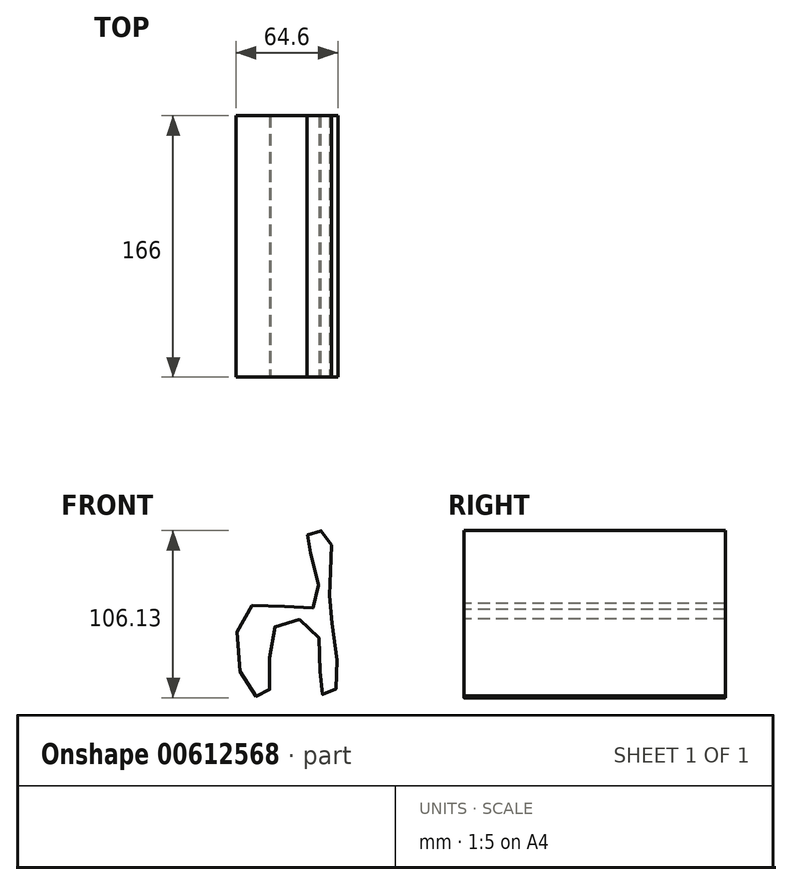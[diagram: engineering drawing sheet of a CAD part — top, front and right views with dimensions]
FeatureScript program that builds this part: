
annotation { "Feature Type Name" : "Feature", "Feature Type Description" : "" }
export const myFeature = defineFeature(function(context is Context, id is Id, definition is map)
    precondition{}
    {
        {
            var Q0;
            Q0=qCreatedBy(makeId("Front.planeOp"),FACE);
            var sketch = newSketch(context, id + "F0", { "sketchPlane" : qUnion([Q0])});
            skFitSpline(sketch, "E0", {"points": [v(44.42, 30.54) * mm, v(44.81, 0) * mm, v(46.61, -46.11) * mm, v(38.43, -46.71) * mm, v(35.03, -7.19) * mm, v(8.88, -4.8) * mm, v(4.7, -47.3) * mm, v(-8.28, -43.92) * mm, v(-7.09, 8.18) * mm, v(33.84, 7.59) * mm, v(31.04, 44.32) * mm, v(30.64, 54.7) * mm, v(41.62, 54.7) * mm, v(44.42, 30.54) * mm]});
            skSolve(sketch);
        }
        {
            var Q0;
            Q0=makeQuery(id+"F0.imprint","IMPRINT",FACE,{"disambiguationData":[TD([[makeQuery(id+"F0.imprint","IMPRINT",EDGE,{"derivedFrom":sQuery(id+"F0.wireOp",EDGE,"E0")}),-1.0]])]});
            var Q1;
            Q1=sQuery(id+"F0.wireOp",EDGE,"E0");
            extrude(context, id + "F1", {"entities" : qUnion([Q0]), "surfaceEntities" : qUnion([Q1]), "depth" : 83 * mm, "offsetDistance" : 25 * mm});
        }
        {
            var Q0;
            Q0=qCreatedBy(makeId("Front.planeOp"),FACE);
            cPlane(context, id + "F2", {"entities" : qUnion([Q0]), "cplaneType" : CPlaneType.OFFSET, "offset" : 83 * mm, "width" : 150 * mm, "height" : 150 * mm});
        }
        {
            var Q0;
            Q0=qCreatedBy(makeId("Front.planeOp"),FACE);
            var sketch = newSketch(context, id + "F3", { "sketchPlane" : qUnion([Q0])});
            skFitSpline(sketch, "E1", {"points": [v(36.58, 31.8) * mm, v(15.55, 35.3) * mm, v(11.66, 7.62) * mm], "startDerivative": vector(-53.94, 21.34) * mm, "endDerivative": vector(2.82, -67.7) * mm});
            skSolve(sketch);
        }
        {
            var Q0;
            Q0=sQuery(id+"F3.wireOp",EDGE,"E1");
            extrude(context, id + "F4", {"bodyType" : ToolBodyType.SURFACE, "surfaceEntities" : qUnion([Q0]), "depth" : 13.1 * mm, "offsetDistance" : 25 * mm});
        }
        {
            var Q0;
            Q0=makeQuery(id+"F1.opExtrude","SWEPT_BODY",BODY,{"disambiguationData":[OSD([sQuery(id+"F0.wireOp",EDGE,"E0")])]});
            var Q1;
            Q1=qCreatedBy(id+"F2.planeOp",FACE);
            mirror(context, id + "F5", {"operationType" : NewBodyOperationType.ADD, "entities" : qUnion([Q0]), "mirrorPlane" : qUnion([Q1])});
        }
        {
            var Q0;
            Q0=makeQuery(id+"F4.opExtrude","SWEPT_BODY",BODY,{"disambiguationData":[OSD([sQuery(id+"F3.wireOp",EDGE,"E1")])]});
            var Q1;
            Q1=qCreatedBy(id+"F2.planeOp",FACE);
            mirror(context, id + "F6", {"entities" : qUnion([Q0]), "mirrorPlane" : qUnion([Q1])});
        }
    });
